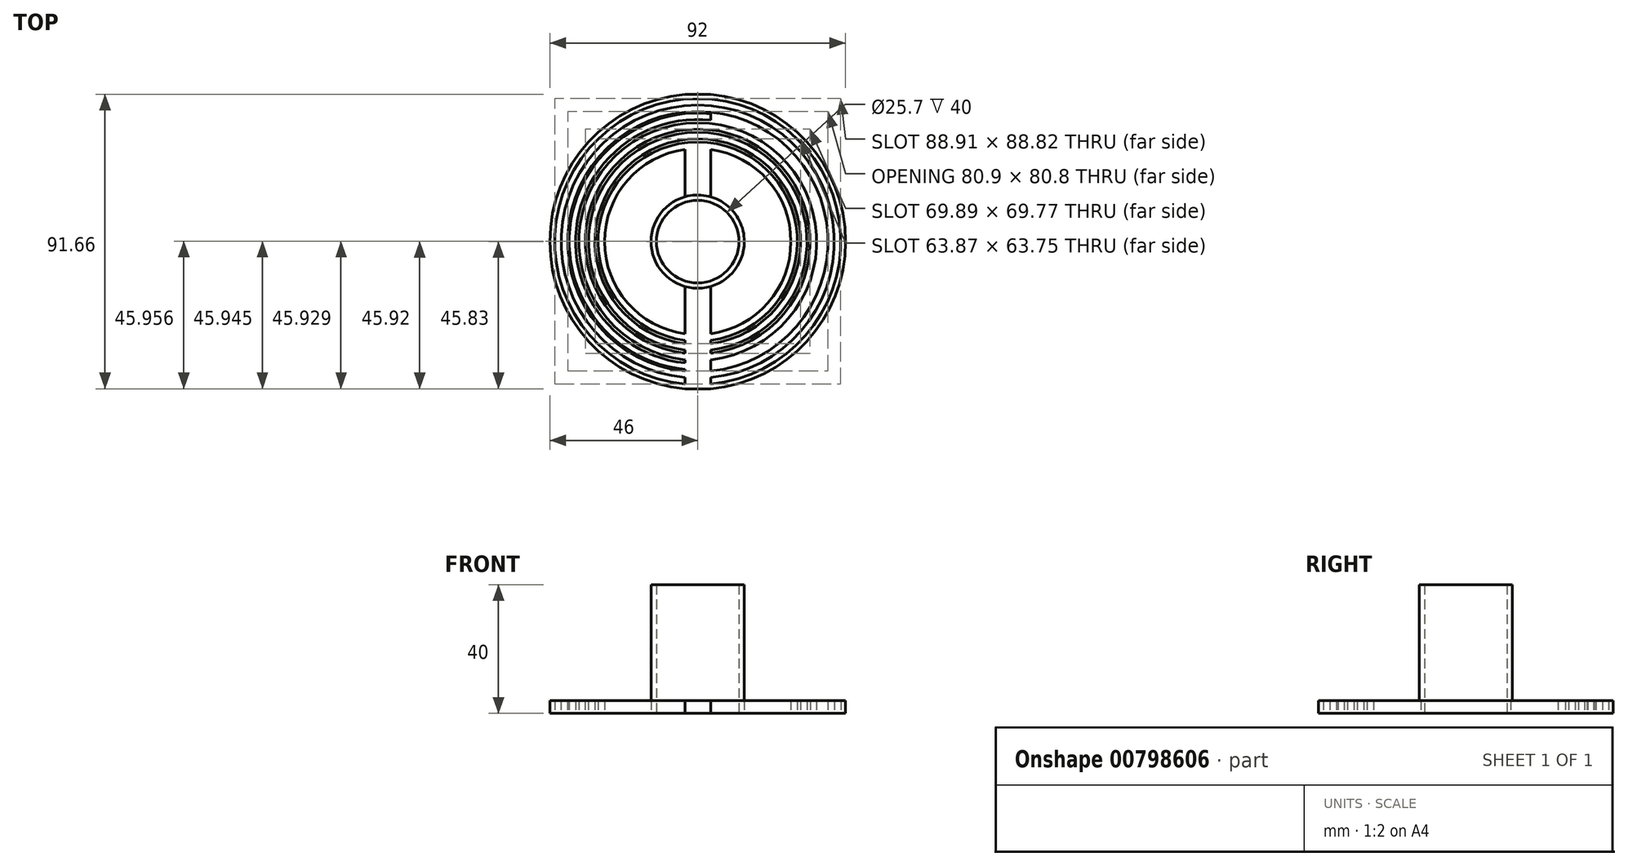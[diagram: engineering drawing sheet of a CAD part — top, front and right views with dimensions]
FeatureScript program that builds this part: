
annotation { "Feature Type Name" : "Feature", "Feature Type Description" : "" }
export const myFeature = defineFeature(function(context is Context, id is Id, definition is map)
    precondition{}
    {
        {
            var Q0;
            Q0=qCreatedBy(makeId("Top.planeOp"),FACE);
            var sketch = newSketch(context, id + "F0", { "sketchPlane" : qUnion([Q0])});
            skCircle(sketch, "E0", {"center": v(0, 0) * mm, "radius": 12.85 * mm});
            skCircle(sketch, "E1", {"center": v(0, 0) * mm, "radius": 14.5 * mm});
            skCircle(sketch, "E2", {"center": v(0, 0) * mm, "radius": 46 * mm});
            skCircle(sketch, "E3", {"center": v(0, 0) * mm, "radius": 44.5 * mm});
            skCircle(sketch, "E4", {"center": v(0, 0) * mm, "radius": 42.5 * mm});
            skCircle(sketch, "E5", {"center": v(0, 0) * mm, "radius": 40.5 * mm});
            skCircle(sketch, "E6", {"center": v(0, 0) * mm, "radius": 40 * mm});
            skCircle(sketch, "E7", {"center": v(0, 0) * mm, "radius": 38 * mm});
            skLineSegment(sketch, "E8.bottom", {"start": v(4, -45.83) * mm, "end": v(-4, -45.83) * mm});
            skLineSegment(sketch, "E8.top", {"start": v(4, 45.83) * mm, "end": v(-4, 45.83) * mm});
            skLineSegment(sketch, "E8.left", {"start": v(4, -45.83) * mm, "end": v(4, 45.83) * mm});
            skLineSegment(sketch, "E8.right", {"start": v(-4, -45.83) * mm, "end": v(-4, 45.83) * mm});
            skCircle(sketch, "E9.0", {"center": v(0, 0) * mm, "radius": 37 * mm});
            skCircle(sketch, "E10.0", {"center": v(0, 0) * mm, "radius": 35 * mm});
            skCircle(sketch, "E11.0", {"center": v(0, 0) * mm, "radius": 34 * mm});
            skCircle(sketch, "E12.0", {"center": v(0, 0) * mm, "radius": 32 * mm});
            skCircle(sketch, "E13.0", {"center": v(0, 0) * mm, "radius": 31 * mm});
            skCircle(sketch, "E14.0", {"center": v(0, 0) * mm, "radius": 29 * mm});
            skSolve(sketch);
        }
        {
            var Q0;
            {var subQ0=sQuery(id+"F0.wireOp",EDGE,"fjfePx7O-aln5-c6GO-I7vF-7R0LJ1V7cihS.top");var subQ1=sQuery(id+"F0.wireOp",EDGE,"E0");var subQ2=makeQuery(id+"F0.imprint","INTERSECT",VERTEX,{"disambiguationData":[OD(0.0)],"derivedFrom":[subQ1,subQ0]});Q0=makeQuery(id+"F0.imprint","IMPRINT",FACE,{"disambiguationData":[TD([[makeQuery(id+"F0.imprint","IMPRINT",EDGE,{"disambiguationData":[TD([[subQ2,1.0]])],"derivedFrom":subQ1}),-1.0]])]});}
            var Q1;
            {var subQ0=sQuery(id+"F0.wireOp",EDGE,"fjfePx7O-aln5-c6GO-I7vF-7R0LJ1V7cihS.top");var subQ1=sQuery(id+"F0.wireOp",EDGE,"E0");var subQ2=makeQuery(id+"F0.imprint","INTERSECT",VERTEX,{"disambiguationData":[OD(0.0)],"derivedFrom":[subQ1,subQ0]});Q1=makeQuery(id+"F0.imprint","IMPRINT",FACE,{"disambiguationData":[TD([[makeQuery(id+"F0.imprint","IMPRINT",EDGE,{"disambiguationData":[TD([[subQ2,-1.0]])],"derivedFrom":subQ1}),-1.0]])]});}
            var Q2;
            {var subQ0=sQuery(id+"F0.wireOp",EDGE,"fjfePx7O-aln5-c6GO-I7vF-7R0LJ1V7cihS.bottom");var subQ1=sQuery(id+"F0.wireOp",EDGE,"E0");var subQ2=makeQuery(id+"F0.imprint","INTERSECT",VERTEX,{"disambiguationData":[OD(0.0)],"derivedFrom":[subQ1,subQ0]});Q2=makeQuery(id+"F0.imprint","IMPRINT",FACE,{"disambiguationData":[TD([[makeQuery(id+"F0.imprint","IMPRINT",EDGE,{"disambiguationData":[TD([[subQ2,-1.0]])],"derivedFrom":subQ1}),-1.0]])]});}
            var Q3;
            {var subQ0=sQuery(id+"F0.wireOp",EDGE,"fjfePx7O-aln5-c6GO-I7vF-7R0LJ1V7cihS.top");var subQ1=sQuery(id+"F0.wireOp",EDGE,"E0");var subQ2=makeQuery(id+"F0.imprint","INTERSECT",VERTEX,{"disambiguationData":[OD(1.0)],"derivedFrom":[subQ1,subQ0]});Q3=makeQuery(id+"F0.imprint","IMPRINT",FACE,{"disambiguationData":[TD([[makeQuery(id+"F0.imprint","IMPRINT",EDGE,{"disambiguationData":[TD([[subQ2,1.0]])],"derivedFrom":subQ1}),-1.0]])]});}
            var Q4;
            {var subQ0=sQuery(id+"F0.wireOp",EDGE,"0ad03920-4a39-4306-b582-f76e78ee916c.4");var subQ1=sQuery(id+"F0.wireOp",EDGE,"E0");var subQ2=makeQuery(id+"F0.imprint","INTERSECT",VERTEX,{"derivedFrom":[subQ1,subQ0]});Q4=makeQuery(id+"F0.imprint","IMPRINT",FACE,{"disambiguationData":[TD([[makeQuery(id+"F0.imprint","IMPRINT",EDGE,{"disambiguationData":[TD([[subQ2,-1.0]])],"derivedFrom":subQ1}),-1.0]])]});}
            var Q5;
            {var subQ0=sQuery(id+"F0.wireOp",EDGE,"fjfePx7O-aln5-c6GO-I7vF-7R0LJ1V7cihS.top");var subQ1=sQuery(id+"F0.wireOp",EDGE,"E0");var subQ2=makeQuery(id+"F0.imprint","INTERSECT",VERTEX,{"disambiguationData":[OD(1.0)],"derivedFrom":[subQ1,subQ0]});Q5=makeQuery(id+"F0.imprint","IMPRINT",FACE,{"disambiguationData":[TD([[makeQuery(id+"F0.imprint","IMPRINT",EDGE,{"disambiguationData":[TD([[subQ2,-1.0]])],"derivedFrom":subQ1}),-1.0]])]});}
            var Q6;
            {var subQ0=sQuery(id+"F0.wireOp",EDGE,"c589fe59-f965-41e5-843e-0e27f58c8ba7.4");var subQ1=sQuery(id+"F0.wireOp",EDGE,"E0");var subQ2=makeQuery(id+"F0.imprint","INTERSECT",VERTEX,{"derivedFrom":[subQ1,subQ0]});Q6=makeQuery(id+"F0.imprint","IMPRINT",FACE,{"disambiguationData":[TD([[makeQuery(id+"F0.imprint","IMPRINT",EDGE,{"disambiguationData":[TD([[subQ2,-1.0]])],"derivedFrom":subQ1}),-1.0]])]});}
            var Q7;
            {var subQ0=sQuery(id+"F0.wireOp",EDGE,"c589fe59-f965-41e5-843e-0e27f58c8ba7.0");var subQ1=sQuery(id+"F0.wireOp",EDGE,"E0");var subQ2=makeQuery(id+"F0.imprint","INTERSECT",VERTEX,{"derivedFrom":[subQ1,subQ0]});Q7=makeQuery(id+"F0.imprint","IMPRINT",FACE,{"disambiguationData":[TD([[makeQuery(id+"F0.imprint","IMPRINT",EDGE,{"disambiguationData":[TD([[subQ2,-1.0]])],"derivedFrom":subQ1}),-1.0]])]});}
            extrude(context, id + "F1", {"entities" : qUnion([Q0, Q1, Q2, Q3, Q4, Q5, Q6, Q7]), "depth" : 40 * mm, "offsetDistance" : 25 * mm});
        }
        {
            var Q0;
            {var subQ0=sQuery(id+"F0.wireOp",EDGE,"E8.right");var subQ1=sQuery(id+"F0.wireOp",EDGE,"E1");var subQ2=makeQuery(id+"F0.imprint","INTERSECT",VERTEX,{"disambiguationData":[OD(1.0)],"derivedFrom":[subQ1,subQ0]});Q0=makeQuery(id+"F0.imprint","IMPRINT",FACE,{"disambiguationData":[TD([[makeQuery(id+"F0.imprint","IMPRINT",EDGE,{"disambiguationData":[TD([[subQ2,-1.0]])],"derivedFrom":subQ1}),-1.0]])]});}
            var Q1;
            {var subQ0=sQuery(id+"F0.wireOp",EDGE,"E8.right");var subQ1=sQuery(id+"F0.wireOp",EDGE,"E4");var subQ2=makeQuery(id+"F0.imprint","INTERSECT",VERTEX,{"disambiguationData":[OD(0.0)],"derivedFrom":[subQ1,subQ0]});Q1=makeQuery(id+"F0.imprint","IMPRINT",FACE,{"disambiguationData":[TD([[makeQuery(id+"F0.imprint","IMPRINT",EDGE,{"disambiguationData":[TD([[subQ2,1.0]])],"derivedFrom":subQ1}),1.0]])]});}
            var Q2;
            {var subQ0=sQuery(id+"F0.wireOp",EDGE,"E8.right");var subQ1=sQuery(id+"F0.wireOp",EDGE,"E4");var subQ2=makeQuery(id+"F0.imprint","INTERSECT",VERTEX,{"disambiguationData":[OD(0.0)],"derivedFrom":[subQ1,subQ0]});Q2=makeQuery(id+"F0.imprint","IMPRINT",FACE,{"disambiguationData":[TD([[makeQuery(id+"F0.imprint","IMPRINT",EDGE,{"disambiguationData":[TD([[subQ2,-1.0]])],"derivedFrom":subQ1}),1.0]])]});}
            var Q3;
            {var subQ0=sQuery(id+"F0.wireOp",EDGE,"E8.right");var subQ1=sQuery(id+"F0.wireOp",EDGE,"E4");var subQ2=makeQuery(id+"F0.imprint","INTERSECT",VERTEX,{"disambiguationData":[OD(1.0)],"derivedFrom":[subQ1,subQ0]});Q3=makeQuery(id+"F0.imprint","IMPRINT",FACE,{"disambiguationData":[TD([[makeQuery(id+"F0.imprint","IMPRINT",EDGE,{"disambiguationData":[TD([[subQ2,-1.0]])],"derivedFrom":subQ1}),1.0]])]});}
            var Q4;
            {var subQ0=sQuery(id+"F0.wireOp",EDGE,"E8.left");var subQ1=sQuery(id+"F0.wireOp",EDGE,"E4");var subQ2=makeQuery(id+"F0.imprint","INTERSECT",VERTEX,{"disambiguationData":[OD(0.0)],"derivedFrom":[subQ1,subQ0]});Q4=makeQuery(id+"F0.imprint","IMPRINT",FACE,{"disambiguationData":[TD([[makeQuery(id+"F0.imprint","IMPRINT",EDGE,{"disambiguationData":[TD([[subQ2,1.0]])],"derivedFrom":subQ1}),1.0]])]});}
            var Q5;
            {var subQ0=sQuery(id+"F0.wireOp",EDGE,"E8.right");var subQ1=sQuery(id+"F0.wireOp",EDGE,"E6");var subQ2=makeQuery(id+"F0.imprint","INTERSECT",VERTEX,{"disambiguationData":[OD(0.0)],"derivedFrom":[subQ1,subQ0]});Q5=makeQuery(id+"F0.imprint","IMPRINT",FACE,{"disambiguationData":[TD([[makeQuery(id+"F0.imprint","IMPRINT",EDGE,{"disambiguationData":[TD([[subQ2,1.0]])],"derivedFrom":subQ1}),1.0]])]});}
            var Q6;
            {var subQ0=sQuery(id+"F0.wireOp",EDGE,"E8.right");var subQ1=sQuery(id+"F0.wireOp",EDGE,"E6");var subQ2=makeQuery(id+"F0.imprint","INTERSECT",VERTEX,{"disambiguationData":[OD(0.0)],"derivedFrom":[subQ1,subQ0]});Q6=makeQuery(id+"F0.imprint","IMPRINT",FACE,{"disambiguationData":[TD([[makeQuery(id+"F0.imprint","IMPRINT",EDGE,{"disambiguationData":[TD([[subQ2,-1.0]])],"derivedFrom":subQ1}),1.0]])]});}
            var Q7;
            {var subQ0=sQuery(id+"F0.wireOp",EDGE,"E8.right");var subQ1=sQuery(id+"F0.wireOp",EDGE,"E6");var subQ2=makeQuery(id+"F0.imprint","INTERSECT",VERTEX,{"disambiguationData":[OD(1.0)],"derivedFrom":[subQ1,subQ0]});Q7=makeQuery(id+"F0.imprint","IMPRINT",FACE,{"disambiguationData":[TD([[makeQuery(id+"F0.imprint","IMPRINT",EDGE,{"disambiguationData":[TD([[subQ2,-1.0]])],"derivedFrom":subQ1}),1.0]])]});}
            var Q8;
            {var subQ0=sQuery(id+"F0.wireOp",EDGE,"E8.left");var subQ1=sQuery(id+"F0.wireOp",EDGE,"E6");var subQ2=makeQuery(id+"F0.imprint","INTERSECT",VERTEX,{"disambiguationData":[OD(0.0)],"derivedFrom":[subQ1,subQ0]});Q8=makeQuery(id+"F0.imprint","IMPRINT",FACE,{"disambiguationData":[TD([[makeQuery(id+"F0.imprint","IMPRINT",EDGE,{"disambiguationData":[TD([[subQ2,1.0]])],"derivedFrom":subQ1}),1.0]])]});}
            var Q9;
            {var subQ0=sQuery(id+"F0.wireOp",EDGE,"E8.right");var subQ1=sQuery(id+"F0.wireOp",EDGE,"E5");var subQ2=makeQuery(id+"F0.imprint","INTERSECT",VERTEX,{"disambiguationData":[OD(1.0)],"derivedFrom":[subQ1,subQ0]});Q9=makeQuery(id+"F0.imprint","IMPRINT",FACE,{"disambiguationData":[TD([[makeQuery(id+"F0.imprint","IMPRINT",EDGE,{"disambiguationData":[TD([[subQ2,-1.0]])],"derivedFrom":subQ1}),1.0]])]});}
            var Q10;
            {var subQ0=sQuery(id+"F0.wireOp",EDGE,"E8.right");var subQ1=sQuery(id+"F0.wireOp",EDGE,"E3");var subQ2=makeQuery(id+"F0.imprint","INTERSECT",VERTEX,{"disambiguationData":[OD(1.0)],"derivedFrom":[subQ1,subQ0]});Q10=makeQuery(id+"F0.imprint","IMPRINT",FACE,{"disambiguationData":[TD([[makeQuery(id+"F0.imprint","IMPRINT",EDGE,{"disambiguationData":[TD([[subQ2,-1.0]])],"derivedFrom":subQ1}),1.0]])]});}
            var Q11;
            {var subQ0=sQuery(id+"F0.wireOp",EDGE,"E8.right");var subQ4=sQuery(id+"F0.wireOp",EDGE,"E3");var subQ6=makeQuery(id+"F0.imprint","INTERSECT",VERTEX,{"disambiguationData":[OD(0.0)],"derivedFrom":[subQ4,subQ0]});Q11=makeQuery(id+"F0.imprint","IMPRINT",FACE,{"disambiguationData":[TD([[makeQuery(id+"F0.imprint","IMPRINT",EDGE,{"disambiguationData":[TD([[subQ6,-1.0]])],"derivedFrom":subQ4}),-1.0]])]});}
            var Q12;
            {var subQ0=sQuery(id+"F0.wireOp",EDGE,"E8.left");var subQ4=sQuery(id+"F0.wireOp",EDGE,"E3");var subQ5=makeQuery(id+"F0.imprint","INTERSECT",VERTEX,{"disambiguationData":[OD(0.0)],"derivedFrom":[subQ4,subQ0]});Q12=makeQuery(id+"F0.imprint","IMPRINT",FACE,{"disambiguationData":[TD([[makeQuery(id+"F0.imprint","IMPRINT",EDGE,{"disambiguationData":[TD([[subQ5,1.0]])],"derivedFrom":subQ4}),-1.0]])]});}
            var Q13;
            {var subQ5=sQuery(id+"F0.wireOp",EDGE,"E8.top");Q13=makeQuery(id+"F0.imprint","IMPRINT",FACE,{"disambiguationData":[TD([[makeQuery(id+"F0.imprint","IMPRINT",EDGE,{"derivedFrom":subQ5}),1.0]])]});}
            var Q14;
            {var subQ5=sQuery(id+"F0.wireOp",EDGE,"E8.bottom");Q14=makeQuery(id+"F0.imprint","IMPRINT",FACE,{"disambiguationData":[TD([[makeQuery(id+"F0.imprint","IMPRINT",EDGE,{"derivedFrom":subQ5}),-1.0]])]});}
            var Q15;
            {var subQ0=sQuery(id+"F0.wireOp",EDGE,"E9.0");var subQ1=sQuery(id+"F0.wireOp",EDGE,"E8.right");var subQ2=makeQuery(id+"F0.imprint","INTERSECT",VERTEX,{"disambiguationData":[OD(0.0)],"derivedFrom":[subQ1,subQ0]});Q15=makeQuery(id+"F0.imprint","IMPRINT",FACE,{"disambiguationData":[TD([[makeQuery(id+"F0.imprint","IMPRINT",EDGE,{"disambiguationData":[TD([[subQ2,-1.0]])],"derivedFrom":subQ1}),1.0]])]});}
            var Q16;
            {var subQ0=sQuery(id+"F0.wireOp",EDGE,"E11.0");var subQ1=sQuery(id+"F0.wireOp",EDGE,"E8.right");var subQ2=makeQuery(id+"F0.imprint","INTERSECT",VERTEX,{"disambiguationData":[OD(0.0)],"derivedFrom":[subQ1,subQ0]});Q16=makeQuery(id+"F0.imprint","IMPRINT",FACE,{"disambiguationData":[TD([[makeQuery(id+"F0.imprint","IMPRINT",EDGE,{"disambiguationData":[TD([[subQ2,-1.0]])],"derivedFrom":subQ1}),1.0]])]});}
            var Q17;
            {var subQ0=sQuery(id+"F0.wireOp",EDGE,"E13.0");var subQ1=sQuery(id+"F0.wireOp",EDGE,"E8.right");var subQ2=makeQuery(id+"F0.imprint","INTERSECT",VERTEX,{"disambiguationData":[OD(0.0)],"derivedFrom":[subQ1,subQ0]});Q17=makeQuery(id+"F0.imprint","IMPRINT",FACE,{"disambiguationData":[TD([[makeQuery(id+"F0.imprint","IMPRINT",EDGE,{"disambiguationData":[TD([[subQ2,-1.0]])],"derivedFrom":subQ1}),1.0]])]});}
            var Q18;
            {var subQ0=sQuery(id+"F0.wireOp",EDGE,"E9.0");var subQ1=sQuery(id+"F0.wireOp",EDGE,"E8.left");var subQ2=makeQuery(id+"F0.imprint","INTERSECT",VERTEX,{"disambiguationData":[OD(0.0)],"derivedFrom":[subQ1,subQ0]});Q18=makeQuery(id+"F0.imprint","IMPRINT",FACE,{"disambiguationData":[TD([[makeQuery(id+"F0.imprint","IMPRINT",EDGE,{"disambiguationData":[TD([[subQ2,-1.0]])],"derivedFrom":subQ1}),-1.0]])]});}
            var Q19;
            {var subQ0=sQuery(id+"F0.wireOp",EDGE,"E11.0");var subQ1=sQuery(id+"F0.wireOp",EDGE,"E8.left");var subQ2=makeQuery(id+"F0.imprint","INTERSECT",VERTEX,{"disambiguationData":[OD(0.0)],"derivedFrom":[subQ1,subQ0]});Q19=makeQuery(id+"F0.imprint","IMPRINT",FACE,{"disambiguationData":[TD([[makeQuery(id+"F0.imprint","IMPRINT",EDGE,{"disambiguationData":[TD([[subQ2,-1.0]])],"derivedFrom":subQ1}),-1.0]])]});}
            var Q20;
            {var subQ0=sQuery(id+"F0.wireOp",EDGE,"E13.0");var subQ1=sQuery(id+"F0.wireOp",EDGE,"E8.left");var subQ2=makeQuery(id+"F0.imprint","INTERSECT",VERTEX,{"disambiguationData":[OD(0.0)],"derivedFrom":[subQ1,subQ0]});Q20=makeQuery(id+"F0.imprint","IMPRINT",FACE,{"disambiguationData":[TD([[makeQuery(id+"F0.imprint","IMPRINT",EDGE,{"disambiguationData":[TD([[subQ2,-1.0]])],"derivedFrom":subQ1}),-1.0]])]});}
            var Q21;
            {var subQ0=sQuery(id+"F0.wireOp",EDGE,"E14.0");var subQ1=sQuery(id+"F0.wireOp",EDGE,"E8.left");var subQ2=makeQuery(id+"F0.imprint","INTERSECT",VERTEX,{"disambiguationData":[OD(1.0)],"derivedFrom":[subQ1,subQ0]});Q21=makeQuery(id+"F0.imprint","IMPRINT",FACE,{"disambiguationData":[TD([[makeQuery(id+"F0.imprint","IMPRINT",EDGE,{"disambiguationData":[TD([[subQ2,-1.0]])],"derivedFrom":subQ1}),1.0]])]});}
            var Q22;
            {var subQ0=sQuery(id+"F0.wireOp",EDGE,"E12.0");var subQ1=sQuery(id+"F0.wireOp",EDGE,"E8.left");var subQ2=makeQuery(id+"F0.imprint","INTERSECT",VERTEX,{"disambiguationData":[OD(1.0)],"derivedFrom":[subQ1,subQ0]});Q22=makeQuery(id+"F0.imprint","IMPRINT",FACE,{"disambiguationData":[TD([[makeQuery(id+"F0.imprint","IMPRINT",EDGE,{"disambiguationData":[TD([[subQ2,-1.0]])],"derivedFrom":subQ1}),1.0]])]});}
            var Q23;
            {var subQ0=sQuery(id+"F0.wireOp",EDGE,"E10.0");var subQ1=sQuery(id+"F0.wireOp",EDGE,"E8.left");var subQ2=makeQuery(id+"F0.imprint","INTERSECT",VERTEX,{"disambiguationData":[OD(1.0)],"derivedFrom":[subQ1,subQ0]});Q23=makeQuery(id+"F0.imprint","IMPRINT",FACE,{"disambiguationData":[TD([[makeQuery(id+"F0.imprint","IMPRINT",EDGE,{"disambiguationData":[TD([[subQ2,-1.0]])],"derivedFrom":subQ1}),1.0]])]});}
            var Q24;
            {var subQ0=sQuery(id+"F0.wireOp",EDGE,"E13.0");var subQ1=sQuery(id+"F0.wireOp",EDGE,"E8.left");var subQ2=makeQuery(id+"F0.imprint","INTERSECT",VERTEX,{"disambiguationData":[OD(0.0)],"derivedFrom":[subQ1,subQ0]});Q24=makeQuery(id+"F0.imprint","IMPRINT",FACE,{"disambiguationData":[TD([[makeQuery(id+"F0.imprint","IMPRINT",EDGE,{"disambiguationData":[TD([[subQ2,-1.0]])],"derivedFrom":subQ1}),1.0]])]});}
            var Q25;
            {var subQ0=sQuery(id+"F0.wireOp",EDGE,"E11.0");var subQ1=sQuery(id+"F0.wireOp",EDGE,"E8.left");var subQ2=makeQuery(id+"F0.imprint","INTERSECT",VERTEX,{"disambiguationData":[OD(0.0)],"derivedFrom":[subQ1,subQ0]});Q25=makeQuery(id+"F0.imprint","IMPRINT",FACE,{"disambiguationData":[TD([[makeQuery(id+"F0.imprint","IMPRINT",EDGE,{"disambiguationData":[TD([[subQ2,-1.0]])],"derivedFrom":subQ1}),1.0]])]});}
            var Q26;
            {var subQ0=sQuery(id+"F0.wireOp",EDGE,"E9.0");var subQ1=sQuery(id+"F0.wireOp",EDGE,"E8.left");var subQ2=makeQuery(id+"F0.imprint","INTERSECT",VERTEX,{"disambiguationData":[OD(0.0)],"derivedFrom":[subQ1,subQ0]});Q26=makeQuery(id+"F0.imprint","IMPRINT",FACE,{"disambiguationData":[TD([[makeQuery(id+"F0.imprint","IMPRINT",EDGE,{"disambiguationData":[TD([[subQ2,-1.0]])],"derivedFrom":subQ1}),1.0]])]});}
            var Q27;
            {var subQ0=sQuery(id+"F0.wireOp",EDGE,"E12.0");var subQ1=sQuery(id+"F0.wireOp",EDGE,"E8.left");var subQ2=makeQuery(id+"F0.imprint","INTERSECT",VERTEX,{"disambiguationData":[OD(0.0)],"derivedFrom":[subQ1,subQ0]});Q27=makeQuery(id+"F0.imprint","IMPRINT",FACE,{"disambiguationData":[TD([[makeQuery(id+"F0.imprint","IMPRINT",EDGE,{"disambiguationData":[TD([[subQ2,-1.0]])],"derivedFrom":subQ1}),1.0]])]});}
            var Q28;
            {var subQ0=sQuery(id+"F0.wireOp",EDGE,"E10.0");var subQ1=sQuery(id+"F0.wireOp",EDGE,"E8.left");var subQ2=makeQuery(id+"F0.imprint","INTERSECT",VERTEX,{"disambiguationData":[OD(0.0)],"derivedFrom":[subQ1,subQ0]});Q28=makeQuery(id+"F0.imprint","IMPRINT",FACE,{"disambiguationData":[TD([[makeQuery(id+"F0.imprint","IMPRINT",EDGE,{"disambiguationData":[TD([[subQ2,-1.0]])],"derivedFrom":subQ1}),1.0]])]});}
            var Q29;
            {var subQ0=sQuery(id+"F0.wireOp",EDGE,"E8.right");var subQ1=sQuery(id+"F0.wireOp",EDGE,"E7");var subQ2=makeQuery(id+"F0.imprint","INTERSECT",VERTEX,{"disambiguationData":[OD(1.0)],"derivedFrom":[subQ1,subQ0]});Q29=makeQuery(id+"F0.imprint","IMPRINT",FACE,{"disambiguationData":[TD([[makeQuery(id+"F0.imprint","IMPRINT",EDGE,{"disambiguationData":[TD([[subQ2,-1.0]])],"derivedFrom":subQ1}),1.0]])]});}
            var Q30;
            {var subQ0=sQuery(id+"F0.wireOp",EDGE,"E8.right");var subQ1=sQuery(id+"F0.wireOp",EDGE,"E1");var subQ2=makeQuery(id+"F0.imprint","INTERSECT",VERTEX,{"disambiguationData":[OD(0.0)],"derivedFrom":[subQ1,subQ0]});Q30=makeQuery(id+"F0.imprint","IMPRINT",FACE,{"disambiguationData":[TD([[makeQuery(id+"F0.imprint","IMPRINT",EDGE,{"disambiguationData":[TD([[subQ2,1.0]])],"derivedFrom":subQ1}),-1.0]])]});}
            extrude(context, id + "F2", {"entities" : qUnion([Q0, Q1, Q2, Q3, Q4, Q5, Q6, Q7, Q8, Q9, Q10, Q11, Q12, Q13, Q14, Q15, Q16, Q17, Q18, Q19, Q20, Q21, Q22, Q23, Q24, Q25, Q26, Q27, Q28, Q29, Q30]), "operationType" : NewBodyOperationType.ADD, "depth" : 4 * mm, "offsetDistance" : 25 * mm});
        }
    });
